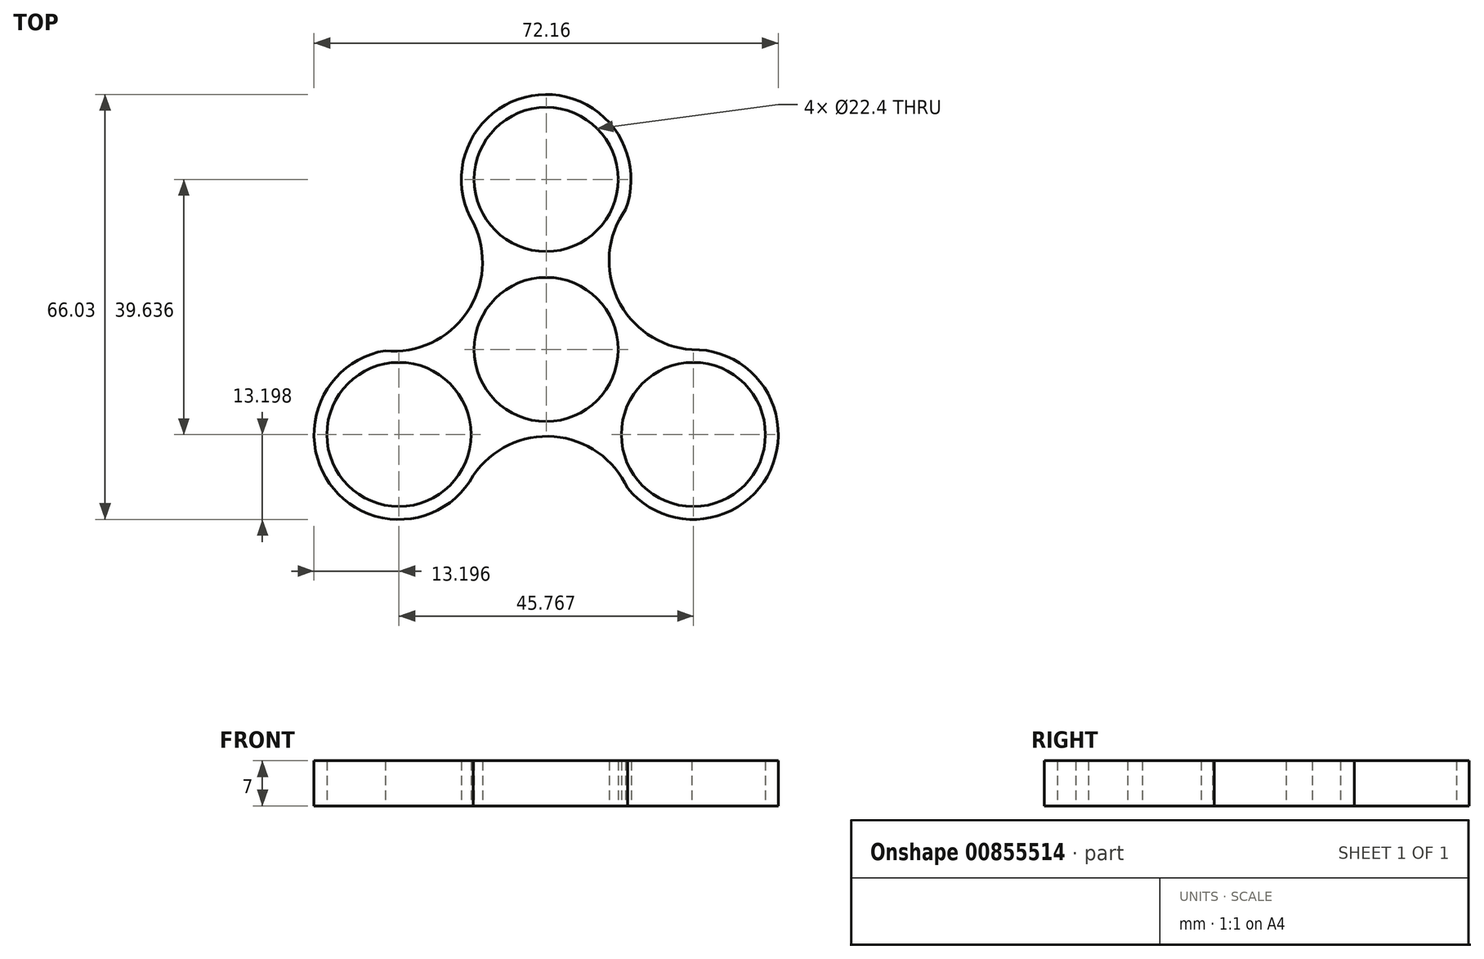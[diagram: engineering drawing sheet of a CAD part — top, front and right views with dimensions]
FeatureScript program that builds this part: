
annotation { "Feature Type Name" : "Feature", "Feature Type Description" : "" }
export const myFeature = defineFeature(function(context is Context, id is Id, definition is map)
    precondition{}
    {
        {
            var Q0;
            Q0=qCreatedBy(makeId("Top.planeOp"),FACE);
            var sketch = newSketch(context, id + "F0", { "sketchPlane" : qUnion([Q0])});
            skCircle(sketch, "E0", {"center": v(0, 0) * mm, "radius": 11.2 * mm});
            skCircle(sketch, "E1", {"center": v(0, 26.42) * mm, "radius": 11.2 * mm});
            skCircle(sketch, "E2", {"center": v(0, 26.42) * mm, "radius": 13.2 * mm});
            skCircle(sketch, "E3.1.0", {"center": v(-22.88, -13.21) * mm, "radius": 11.2 * mm});
            skCircle(sketch, "E3.1.1", {"center": v(-22.88, -13.21) * mm, "radius": 13.2 * mm});
            skCircle(sketch, "E3.2.0", {"center": v(22.88, -13.21) * mm, "radius": 11.2 * mm});
            skCircle(sketch, "E3.2.1", {"center": v(22.88, -13.21) * mm, "radius": 13.2 * mm});
            skArc(sketch, "E4", {"start": v(12.34, 21.75) * mm, "mid": v(11.1, 7.85) * mm, "end": v(22.63, -0.01) * mm});
            skArc(sketch, "E5.1.0", {"start": v(-25, -0.18) * mm, "mid": v(-12.35, 5.69) * mm, "end": v(-11.3, 19.6) * mm});
            skArc(sketch, "E5.2.0", {"start": v(12.66, -21.56) * mm, "mid": v(1.25, -13.54) * mm, "end": v(-11.33, -19.59) * mm});
            skSolve(sketch);
        }
        {
            var Q0;
            Q0=makeQuery(id+"F0.imprint","IMPRINT",FACE,{"disambiguationData":[TD([[makeQuery(id+"F0.imprint","IMPRINT",EDGE,{"derivedFrom":sQuery(id+"F0.wireOp",EDGE,"E0")}),-1.0]])]});
            var Q1;
            Q1=makeQuery(id+"F0.imprint","IMPRINT",FACE,{"disambiguationData":[TD([[makeQuery(id+"F0.imprint","IMPRINT",EDGE,{"derivedFrom":sQuery(id+"F0.wireOp",EDGE,"E3.2.0")}),-1.0]])]});
            var Q2;
            Q2=makeQuery(id+"F0.imprint","IMPRINT",FACE,{"disambiguationData":[TD([[makeQuery(id+"F0.imprint","IMPRINT",EDGE,{"derivedFrom":sQuery(id+"F0.wireOp",EDGE,"E3.1.0")}),-1.0]])]});
            var Q3;
            Q3=makeQuery(id+"F0.imprint","IMPRINT",FACE,{"disambiguationData":[TD([[makeQuery(id+"F0.imprint","IMPRINT",EDGE,{"derivedFrom":sQuery(id+"F0.wireOp",EDGE,"E1")}),-1.0]])]});
            extrude(context, id + "F1", {"entities" : qUnion([Q0, Q1, Q2, Q3]), "depth" : 7 * mm, "offsetDistance" : 25 * mm});
        }
    });
